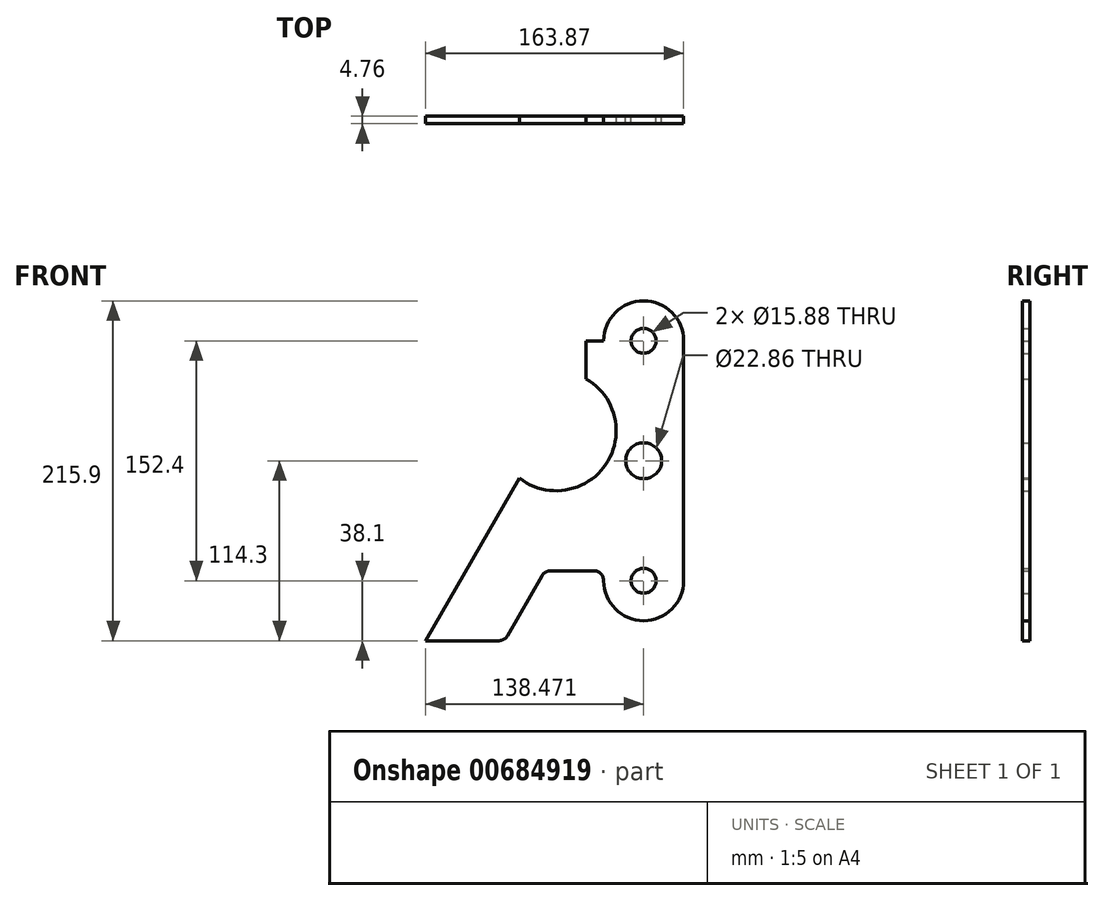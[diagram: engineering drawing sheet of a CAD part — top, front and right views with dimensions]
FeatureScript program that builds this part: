
annotation { "Feature Type Name" : "Feature", "Feature Type Description" : "" }
export const myFeature = defineFeature(function(context is Context, id is Id, definition is map)
    precondition{}
    {
        {
            var Q0;
            Q0=qCreatedBy(makeId("Front.planeOp"),FACE);
            var sketch = newSketch(context, id + "F0", { "sketchPlane" : qUnion([Q0])});
            skLineSegment(sketch, "E0", {"start": v(19, 57.15) * mm, "end": v(30.12, 57.15) * mm});
            skLineSegment(sketch, "E1", {"start": v(80.92, 57.15) * mm, "end": v(80.92, -95.25) * mm});
            skLineSegment(sketch, "E2", {"start": v(19, 57.15) * mm, "end": v(19, 33.02) * mm});
            skArc(sketch, "E3", {"start": v(19, 33.02) * mm, "mid": v(31.64, -21.22) * mm, "end": v(-23.34, -30.11) * mm});
            skArc(sketch, "E4", {"start": v(30.12, 57.15) * mm, "mid": v(55.52, 82.55) * mm, "end": v(80.92, 57.15) * mm});
            skCircle(sketch, "E5", {"center": v(55.52, 57.15) * mm, "radius": 7.94 * mm});
            skArc(sketch, "E6.MirrorCS", {"start": v(30.12, -95.25) * mm, "mid": v(55.52, -120.65) * mm, "end": v(80.92, -95.25) * mm});
            skCircle(sketch, "E7.MirrorC", {"center": v(55.52, -95.25) * mm, "radius": 7.94 * mm});
            skLineSegment(sketch, "E8", {"start": v(23.77, -88.9) * mm, "end": v(-3.5, -88.9) * mm});
            skLineSegment(sketch, "E9", {"start": v(-9, -92.07) * mm, "end": v(-31, -130.18) * mm});
            skPoint(sketch, "E10.visualSharp", {"position": v(30.93, -88.9) * mm});
            skArc(sketch, "E10.filletArc", {"start": v(30.12, -95.25) * mm, "mid": v(28.26, -90.76) * mm, "end": v(23.77, -88.9) * mm});
            skPoint(sketch, "E11.visualSharp", {"position": v(-7.17, -88.9) * mm});
            skArc(sketch, "E11.filletArc", {"start": v(-3.5, -88.9) * mm, "mid": v(-6.68, -89.75) * mm, "end": v(-9, -92.07) * mm});
            skLineSegment(sketch, "E12", {"start": v(-23.34, -30.11) * mm, "end": v(-82.95, -133.35) * mm});
            skLineSegment(sketch, "E13", {"start": v(-82.95, -133.35) * mm, "end": v(-36.5, -133.35) * mm});
            skLineSegment(sketch, "E14", {"start": v(55.52, 82.55) * mm, "end": v(55.52, -120.65) * mm, "construction": true});
            skPoint(sketch, "E14.startSnap0", {"position": v(55.52, 82.55) * mm});
            skLineSegment(sketch, "E15", {"start": v(-23.34, -30.11) * mm, "end": v(19, 33.02) * mm, "construction": true});
            skLineSegment(sketch, "E16", {"start": v(-111.48, -49.16) * mm, "end": v(99.09, -49.16) * mm, "construction": true});
            skPoint(sketch, "E17.visualSharp", {"position": v(-32.84, -133.35) * mm});
            skArc(sketch, "E17.filletArc", {"start": v(-36.5, -133.35) * mm, "mid": v(-33.33, -132.5) * mm, "end": v(-31, -130.18) * mm});
            skCircle(sketch, "E18", {"center": v(55.52, -19.05) * mm, "radius": 11.43 * mm});
            skLineSegment(sketch, "E19", {"start": v(4.66, 57.15) * mm, "end": v(90.42, 57.15) * mm, "construction": true});
            skLineSegment(sketch, "E20", {"start": v(80.92, -95.25) * mm, "end": v(14.37, -95.25) * mm, "construction": true});
            skSolve(sketch);
        }
        {
            var Q0;
            Q0 = qSketchRegion(id + "F0", true);
            extrude(context, id + "F1", {"entities" : qUnion([Q0]), "depth" : 4.76 * mm, "offsetDistance" : 25.4 * mm});
        }
    });
